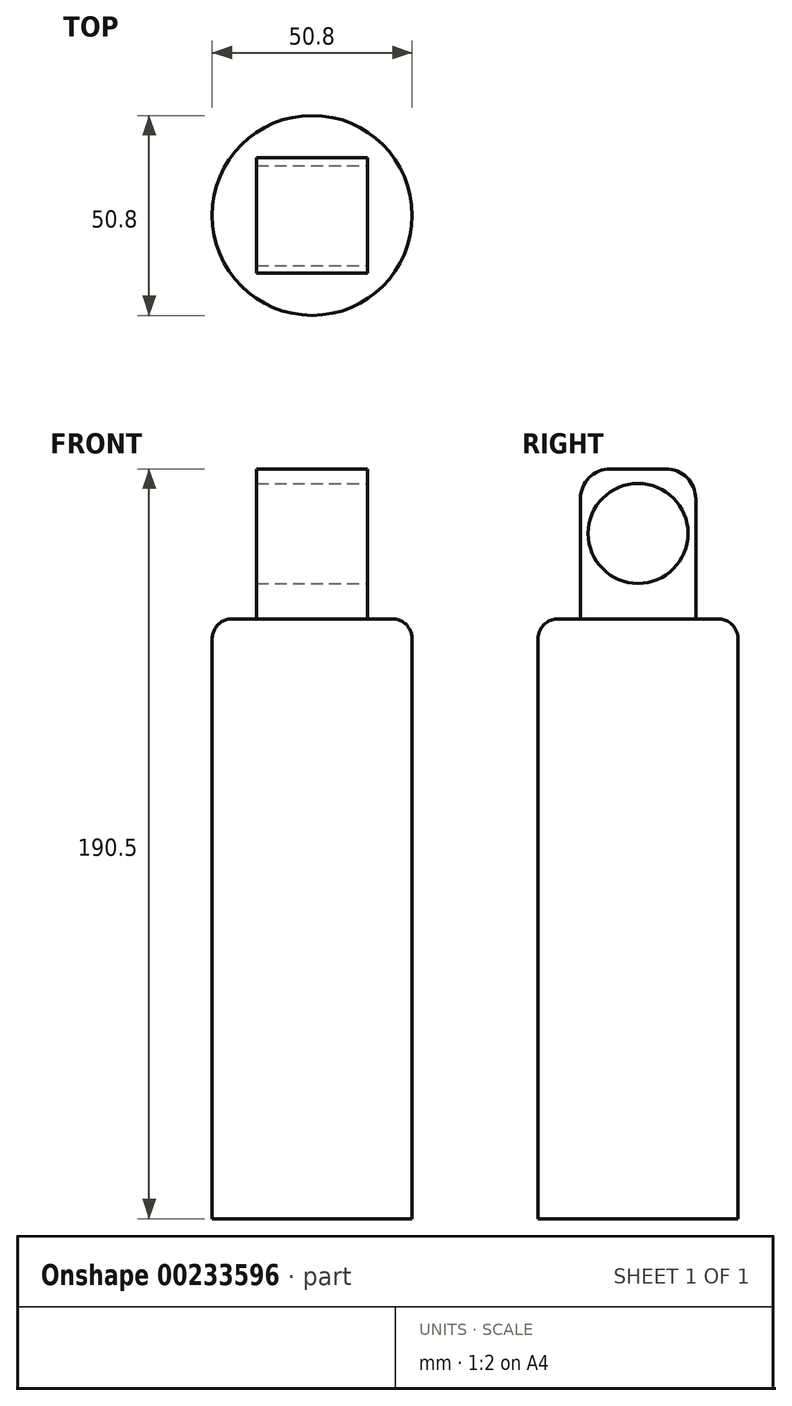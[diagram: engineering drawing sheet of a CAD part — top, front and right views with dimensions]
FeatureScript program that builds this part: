
annotation { "Feature Type Name" : "Feature", "Feature Type Description" : "" }
export const myFeature = defineFeature(function(context is Context, id is Id, definition is map)
    precondition{}
    {
        {
            var Q0;
            Q0=qCreatedBy(makeId("Top.planeOp"),FACE);
            var sketch = newSketch(context, id + "F0", { "sketchPlane" : qUnion([Q0])});
            skCircle(sketch, "E0", {"center": v(0, 0) * mm, "radius": 25.4 * mm});
            skSolve(sketch);
        }
        {
            var Q0;
            Q0=qSketchRegion(id+"F0",true);
            extrude(context, id + "F1", {"entities" : qUnion([Q0]), "depth" : 152.4 * mm});
        }
        {
            var Q0;
            Q0=makeQuery(id+"F1.opExtrude","CAP_EDGE",EDGE,{"disambiguationData":[OSD([sQuery(id+"F0.wireOp",EDGE,"E0")])],"isStart":false});
            fillet(context, id + "F2", {"entities" : qUnion([Q0]), "radius" : 5.08 * mm, "tangentPropagation" : true, "allowEdgeOverflow" : false});
        }
        {
            var Q0;
            Q0=makeQuery(id+"F1.opExtrude","CAP_FACE",FACE,{"disambiguationData":[OSD([sQuery(id+"F0.wireOp",EDGE,"E0")])],"isStart":false});
            var sketch = newSketch(context, id + "F3", { "sketchPlane" : qUnion([Q0])});
            skLineSegment(sketch, "E1.bottom", {"start": v(14.08, -14.65) * mm, "end": v(-14.08, -14.65) * mm});
            skLineSegment(sketch, "E1.top", {"start": v(14.08, 14.65) * mm, "end": v(-14.08, 14.65) * mm});
            skLineSegment(sketch, "E1.left", {"start": v(14.08, -14.65) * mm, "end": v(14.08, 14.65) * mm});
            skLineSegment(sketch, "E1.right", {"start": v(-14.08, -14.65) * mm, "end": v(-14.08, 14.65) * mm});
            skPoint(sketch, "E1.middle", {"position": v(0, 0) * mm});
            skSolve(sketch);
        }
        {
            var Q0;
            Q0=makeQuery(id+"F3.imprint","IMPRINT",FACE,{"disambiguationData":[TD([[makeQuery(id+"F3.imprint","IMPRINT",EDGE,{"derivedFrom":sQuery(id+"F3.wireOp",EDGE,"E1.bottom")}),-1.0]])]});
            extrude(context, id + "F4", {"entities" : qUnion([Q0]), "operationType" : NewBodyOperationType.ADD, "depth" : 38.1 * mm});
        }
        {
            var Q0;
            Q0=makeQuery(id+"F4.opExtrude","SWEPT_FACE",FACE,{"disambiguationData":[OSD([sQuery(id+"F3.wireOp",EDGE,"E1.left")])]});
            var sketch = newSketch(context, id + "F5", { "sketchPlane" : qUnion([Q0])});
            skCircle(sketch, "E2", {"center": v(0, 174.1) * mm, "radius": 12.7 * mm});
            skSolve(sketch);
        }
        {
            var Q0;
            Q0=makeQuery(id+"F4.opExtrude","CAP_EDGE",EDGE,{"disambiguationData":[OSD([sQuery(id+"F3.wireOp",EDGE,"E1.bottom")])],"isStart":false});
            var Q1;
            Q1=makeQuery(id+"F4.opExtrude","CAP_EDGE",EDGE,{"disambiguationData":[OSD([sQuery(id+"F3.wireOp",EDGE,"E1.top")])],"isStart":false});
            fillet(context, id + "F6", {"entities" : qUnion([Q0, Q1]), "radius" : 7.62 * mm, "tangentPropagation" : true, "allowEdgeOverflow" : false});
        }
        {
            var Q0;
            Q0=makeQuery(id+"F5.imprint","IMPRINT",FACE,{"disambiguationData":[TD([[makeQuery(id+"F5.imprint","IMPRINT",EDGE,{"derivedFrom":sQuery(id+"F5.wireOp",EDGE,"E2")}),1.0]])]});
            extrude(context, id + "F7", {"entities" : qUnion([Q0]), "operationType" : NewBodyOperationType.REMOVE, "endBound" : BoundingType.THROUGH_ALL, "oppositeDirection" : true, "depth" : 25.4 * mm});
        }
    });
